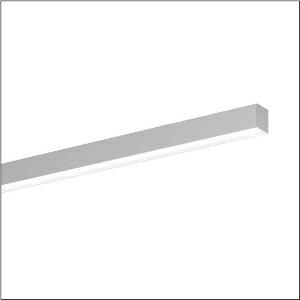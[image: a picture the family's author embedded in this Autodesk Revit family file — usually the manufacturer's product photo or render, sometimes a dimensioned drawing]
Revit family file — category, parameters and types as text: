
# Revit family: silica_21_51mx23tat4s
name_source: partatom
category: Lighting Fixtures
units: mm (PartAtom-declared; Revit-internal decimal feet)

## family parameters
Cut with Voids When Loaded = No
Host = Face
Light Source = No
Part Type = Normal
Room Calculation Point = No
Round Connector Dimension = Use Diameter
Shared = No

## types (1)
- --- (1 x LED, 3230 lm, 32.4 W, 6500K)
    Apparent Load = 32 VA
    CIE Flux Codes = 78 96 99 100 100
    Color Rendering = 80
    Color Temperature = 6500K
    Default Elevation = 1800 mm
    Description = Silica 21, office luminaire, primary optical cover: prismatic diffuser, of PMMA, CAT 2 (L<= 3000cd/m²), light emission: direct distribution, primary light characteristic: symmetric, installation type: surface-mounted, LED, rated luminous flux: 3.230lm, luminous efficacy: 95lm/W, light colour: 8tw, colour temperature: 2700..6500K, control gear: DALI DT8, with terminal, 3+2-pole, max. 2.5mm², mains connection: 220..240V, AC, 50/60Hz, rated input power: 34W, luminaire housing, of aluminium, metallic grey (RAL 9006), length: 1.204mm, width: 53mm, height: 53mm, protection rating (complete): IP20, insulation class (complete): insulation class I (protective earthing), certification: CE, permissible operating ambient temperature: 0..+35°C, standard: EN 50419, packaging unit: 1 piece
    Height = 53 mm
    Lamp = 1 x LED
    Lamp Light Flux = 3230 lm
    Lamp Power = 32.4 W
    Lamp count = 1
    Length = 1204 mm
    Luminous efficacy = 100 lm/W
    Manufacturer = Siteco
    ModVariant = No
    Model = 51MX23TAT4S
    Mounting Place = Ceiling
    Mounting Type = Surface mounted
    Number of Poles = 1
    OnlyDefault = Yes
    Power Factor = 1
    Product Name = Silica 21
    Product group = office luminaire | ceiling mounted
    ProductGroupID = 301
    Protection Class = Protection class I
    Protection Degree = IP 20
    RLX_Detail_Level = 1
    RLX_Emergency_Light_Flux = 0 lm
    RLX_Emergency_Type = 0
    RLX_Emergency_Type_DB = No
    RlxData = <blob elided: 17961 chars, md5=b42b1339>
    Socket = socket
    Standby Power = 0 W
    System Light Flux = 3230 lm
    System Power = 32 W
    Type Comments = individual setting
    Type Image = l_1335933.jpg
    URL = http://relux.com
    VarID = @adj_140851
    Voltage = 0 V
    Weight = 0.00 kg
    Width = 53 mm

## geometry (parser evidence)
native form markers: Blend x4, Sweep x12
no freeform markers — native parametric forms only
